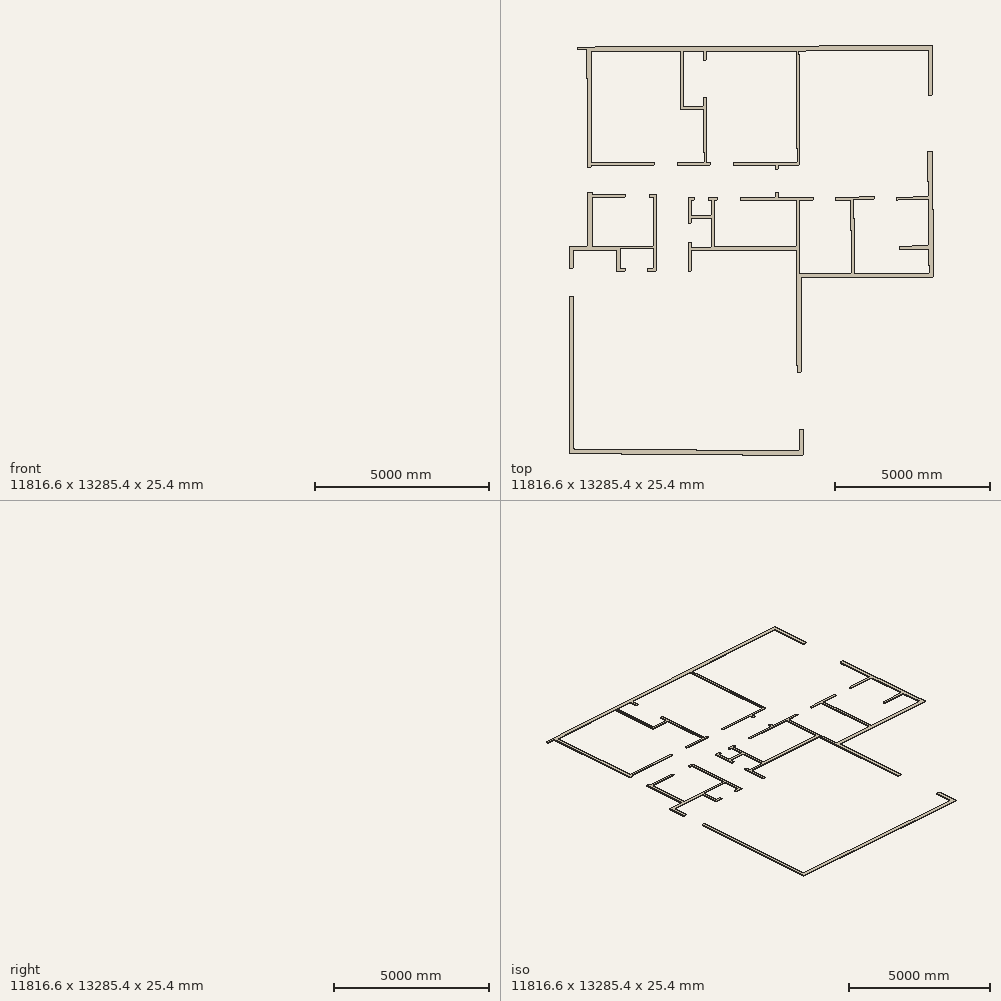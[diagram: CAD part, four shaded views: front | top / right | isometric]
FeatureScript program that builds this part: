
annotation { "Feature Type Name" : "Feature", "Feature Type Description" : "" }
export const myFeature = defineFeature(function(context is Context, id is Id, definition is map)
    precondition{}
    {
        {
            var Q0;
            Q0=qCreatedBy(makeId("Top.planeOp"),FACE);
            var sketch = newSketch(context, id + "F0", { "sketchPlane" : qUnion([Q0])});
            skLineSegment(sketch, "E0", {"start": v(-3431.17, -188.14) * mm, "end": v(3883.78, -248.2) * mm});
            skLineSegment(sketch, "E1", {"start": v(-3431.17, -188.14) * mm, "end": v(-3431.17, 4762.64) * mm});
            skLineSegment(sketch, "E2", {"start": v(-3568.5, 4762.64) * mm, "end": v(-3568.5, -336.6) * mm});
            skLineSegment(sketch, "E3", {"start": v(-3568.5, -336.6) * mm, "end": v(4029.87, -399) * mm});
            skLineSegment(sketch, "E4", {"start": v(4029.87, -399) * mm, "end": v(4029.87, 458) * mm});
            skLineSegment(sketch, "E5", {"start": v(4029.87, 458) * mm, "end": v(3883.78, 459.2) * mm});
            skLineSegment(sketch, "E6", {"start": v(3883.78, -248.2) * mm, "end": v(3883.78, 459.2) * mm});
            skLineSegment(sketch, "E7", {"start": v(-3568.5, 4762.64) * mm, "end": v(-3431.17, 4762.64) * mm});
            skLineSegment(sketch, "E8", {"start": v(-3577.11, 5654.75) * mm, "end": v(-3441.63, 5654.75) * mm});
            skLineSegment(sketch, "E9", {"start": v(-3441.63, 5654.75) * mm, "end": v(-3441.63, 6255.3) * mm});
            skLineSegment(sketch, "E10", {"start": v(-3441.63, 6255.3) * mm, "end": v(-2039.15, 6255.3) * mm});
            skLineSegment(sketch, "E11", {"start": v(-2039.15, 6255.3) * mm, "end": v(-2039.15, 5570.53) * mm});
            skLineSegment(sketch, "E12", {"start": v(-2039.15, 5570.53) * mm, "end": v(-1759.02, 5570.53) * mm});
            skLineSegment(sketch, "E13", {"start": v(-1759.02, 5570.53) * mm, "end": v(-1759.02, 5667.57) * mm});
            skLineSegment(sketch, "E14", {"start": v(-1759.02, 5667.57) * mm, "end": v(-1925.63, 5667.57) * mm});
            skLineSegment(sketch, "E15", {"start": v(-1925.63, 5667.57) * mm, "end": v(-1925.63, 6301.06) * mm});
            skLineSegment(sketch, "E16", {"start": v(-1925.63, 6301.06) * mm, "end": v(-847.22, 6301.06) * mm});
            skLineSegment(sketch, "E17", {"start": v(-847.22, 6301.06) * mm, "end": v(-847.22, 5667.57) * mm});
            skLineSegment(sketch, "E18", {"start": v(-847.22, 5667.57) * mm, "end": v(-1022.99, 5667.57) * mm});
            skLineSegment(sketch, "E19", {"start": v(-1022.99, 5667.57) * mm, "end": v(-1022.99, 5574.2) * mm});
            skLineSegment(sketch, "E20", {"start": v(-1022.99, 5574.2) * mm, "end": v(-755.67, 5574.2) * mm});
            skLineSegment(sketch, "E21", {"start": v(-755.67, 5574.2) * mm, "end": v(-755.67, 8062.4) * mm});
            skLineSegment(sketch, "E22", {"start": v(-755.67, 8062.4) * mm, "end": v(-964.4, 8062.4) * mm});
            skLineSegment(sketch, "E23", {"start": v(-964.4, 8062.4) * mm, "end": v(-964.4, 7972.69) * mm});
            skLineSegment(sketch, "E24", {"start": v(-964.4, 7972.69) * mm, "end": v(-850.88, 7972.69) * mm});
            skLineSegment(sketch, "E25", {"start": v(-850.88, 7972.69) * mm, "end": v(-850.88, 6388.47) * mm});
            skLineSegment(sketch, "E26", {"start": v(-850.88, 6388.47) * mm, "end": v(-2831.49, 6388.47) * mm});
            skLineSegment(sketch, "E27", {"start": v(-2831.49, 6388.47) * mm, "end": v(-2831.49, 7972.69) * mm});
            skLineSegment(sketch, "E28", {"start": v(-2831.49, 7972.69) * mm, "end": v(-1753.73, 7972.69) * mm});
            skLineSegment(sketch, "E29", {"start": v(-1753.73, 7972.69) * mm, "end": v(-1753.73, 8062.4) * mm});
            skLineSegment(sketch, "E30", {"start": v(-1753.73, 8062.4) * mm, "end": v(-2831.49, 8062.4) * mm});
            skLineSegment(sketch, "E31", {"start": v(-2831.49, 8062.4) * mm, "end": v(-2831.49, 8138.6) * mm});
            skLineSegment(sketch, "E32", {"start": v(-2831.49, 8138.6) * mm, "end": v(-2973.3, 8138.6) * mm});
            skLineSegment(sketch, "E33", {"start": v(-2973.3, 8138.6) * mm, "end": v(-2973.3, 6388.47) * mm});
            skLineSegment(sketch, "E34", {"start": v(-2973.3, 6388.47) * mm, "end": v(-3577.11, 6388.47) * mm});
            skLineSegment(sketch, "E35", {"start": v(-3577.11, 6388.47) * mm, "end": v(-3577.11, 5654.75) * mm});
            skLineSegment(sketch, "E36", {"start": v(3806.17, 2284.05) * mm, "end": v(3953.5, 2284.05) * mm});
            skLineSegment(sketch, "E37", {"start": v(3953.5, 2284.05) * mm, "end": v(3953.5, 5361.25) * mm});
            skLineSegment(sketch, "E38", {"start": v(3953.5, 5361.25) * mm, "end": v(8239.48, 5361.25) * mm});
            skLineSegment(sketch, "E39", {"start": v(8239.48, 5361.25) * mm, "end": v(8189.25, 9456.38) * mm});
            skLineSegment(sketch, "E40", {"start": v(8189.25, 9456.38) * mm, "end": v(8038.6, 9454.53) * mm});
            skLineSegment(sketch, "E41", {"start": v(8038.6, 9454.53) * mm, "end": v(8056.64, 7983.25) * mm});
            skLineSegment(sketch, "E42", {"start": v(8056.64, 7983.25) * mm, "end": v(7020.93, 7970.55) * mm});
            skLineSegment(sketch, "E43", {"start": v(7020.93, 7970.55) * mm, "end": v(7022.05, 7879.33) * mm});
            skLineSegment(sketch, "E44", {"start": v(7022.05, 7879.33) * mm, "end": v(8056.64, 7892.01) * mm});
            skLineSegment(sketch, "E45", {"start": v(8056.64, 7892.01) * mm, "end": v(8075, 6396.03) * mm});
            skLineSegment(sketch, "E46", {"start": v(8075, 6396.03) * mm, "end": v(7131.33, 6384.46) * mm});
            skLineSegment(sketch, "E47", {"start": v(7131.33, 6384.46) * mm, "end": v(7132.47, 6292.09) * mm});
            skLineSegment(sketch, "E48", {"start": v(7132.47, 6292.09) * mm, "end": v(8056.64, 6292.09) * mm});
            skLineSegment(sketch, "E49", {"start": v(8056.64, 6292.09) * mm, "end": v(8095.5, 5495.19) * mm});
            skLineSegment(sketch, "E50", {"start": v(8095.5, 5495.19) * mm, "end": v(5674.59, 5495.19) * mm});
            skLineSegment(sketch, "E51", {"start": v(5674.59, 5495.19) * mm, "end": v(5645.19, 7892.01) * mm});
            skLineSegment(sketch, "E52", {"start": v(5645.19, 7892.01) * mm, "end": v(6304.1, 7892.01) * mm});
            skLineSegment(sketch, "E53", {"start": v(6304.1, 7892.01) * mm, "end": v(6302.97, 7983.25) * mm});
            skLineSegment(sketch, "E54", {"start": v(6302.97, 7983.25) * mm, "end": v(5059.47, 7968) * mm});
            skLineSegment(sketch, "E55", {"start": v(5059.47, 7968) * mm, "end": v(5060.58, 7878.2) * mm});
            skLineSegment(sketch, "E56", {"start": v(5060.58, 7878.2) * mm, "end": v(5543.43, 7878.2) * mm});
            skLineSegment(sketch, "E57", {"start": v(5543.43, 7878.2) * mm, "end": v(5572.66, 5495.19) * mm});
            skLineSegment(sketch, "E58", {"start": v(5572.66, 5495.19) * mm, "end": v(3901.21, 5495.19) * mm});
            skLineSegment(sketch, "E59", {"start": v(3901.21, 5495.19) * mm, "end": v(3882.25, 7873.19) * mm});
            skLineSegment(sketch, "E60", {"start": v(3882.25, 7873.19) * mm, "end": v(4356.11, 7879) * mm});
            skLineSegment(sketch, "E61", {"start": v(4356.11, 7879) * mm, "end": v(4355.02, 7967.98) * mm});
            skLineSegment(sketch, "E62", {"start": v(4355.02, 7967.98) * mm, "end": v(3197.25, 7967.98) * mm});
            skLineSegment(sketch, "E63", {"start": v(3197.25, 7967.98) * mm, "end": v(3195.39, 8119.58) * mm});
            skLineSegment(sketch, "E64", {"start": v(3195.39, 8119.58) * mm, "end": v(3102.47, 8118.44) * mm});
            skLineSegment(sketch, "E65", {"start": v(3102.47, 8118.44) * mm, "end": v(3102.47, 7967.98) * mm});
            skLineSegment(sketch, "E66", {"start": v(3102.47, 7967.98) * mm, "end": v(1985.22, 7967.98) * mm});
            skLineSegment(sketch, "E67", {"start": v(1985.22, 7967.98) * mm, "end": v(1986.3, 7879) * mm});
            skLineSegment(sketch, "E68", {"start": v(1986.3, 7879) * mm, "end": v(3790, 7873.19) * mm});
            skLineSegment(sketch, "E69", {"start": v(3790, 7873.19) * mm, "end": v(3790, 6384.46) * mm});
            skLineSegment(sketch, "E70", {"start": v(3790, 6384.46) * mm, "end": v(1127.2, 6384.46) * mm});
            skLineSegment(sketch, "E71", {"start": v(1127.2, 6384.46) * mm, "end": v(1127.2, 7873.19) * mm});
            skLineSegment(sketch, "E72", {"start": v(1127.2, 7873.19) * mm, "end": v(1231.35, 7873.19) * mm});
            skLineSegment(sketch, "E73", {"start": v(1231.35, 7873.19) * mm, "end": v(1230.2, 7967.98) * mm});
            skLineSegment(sketch, "E74", {"start": v(1230.2, 7967.98) * mm, "end": v(931.65, 7967.98) * mm});
            skLineSegment(sketch, "E75", {"start": v(931.65, 7967.98) * mm, "end": v(932.82, 7873.19) * mm});
            skLineSegment(sketch, "E76", {"start": v(932.82, 7873.19) * mm, "end": v(1029.43, 7873.19) * mm});
            skLineSegment(sketch, "E77", {"start": v(1029.43, 7873.19) * mm, "end": v(1035.46, 7381.09) * mm});
            skLineSegment(sketch, "E78", {"start": v(1035.46, 7381.09) * mm, "end": v(389.64, 7381.09) * mm});
            skLineSegment(sketch, "E79", {"start": v(389.64, 7381.09) * mm, "end": v(389.64, 7873.19) * mm});
            skLineSegment(sketch, "E80", {"start": v(389.64, 7873.19) * mm, "end": v(490.6, 7873.19) * mm});
            skLineSegment(sketch, "E81", {"start": v(490.6, 7873.19) * mm, "end": v(489.44, 7967.98) * mm});
            skLineSegment(sketch, "E82", {"start": v(489.44, 7967.98) * mm, "end": v(290.8, 7967.98) * mm});
            skLineSegment(sketch, "E83", {"start": v(290.8, 7967.98) * mm, "end": v(301.4, 7104.7) * mm});
            skLineSegment(sketch, "E84", {"start": v(301.4, 7104.7) * mm, "end": v(391.77, 7104.7) * mm});
            skLineSegment(sketch, "E85", {"start": v(391.77, 7104.7) * mm, "end": v(391.77, 7288.53) * mm});
            skLineSegment(sketch, "E86", {"start": v(391.77, 7288.53) * mm, "end": v(1035.46, 7288.53) * mm});
            skLineSegment(sketch, "E87", {"start": v(1035.46, 7288.53) * mm, "end": v(1035.46, 6337.35) * mm});
            skLineSegment(sketch, "E88", {"start": v(1035.46, 6337.35) * mm, "end": v(398.15, 6337.35) * mm});
            skLineSegment(sketch, "E89", {"start": v(398.15, 6337.35) * mm, "end": v(398.15, 6514.83) * mm});
            skLineSegment(sketch, "E90", {"start": v(398.15, 6514.83) * mm, "end": v(299.3, 6514.83) * mm});
            skLineSegment(sketch, "E91", {"start": v(299.3, 6514.83) * mm, "end": v(299.3, 5548.78) * mm});
            skLineSegment(sketch, "E92", {"start": v(299.3, 5548.78) * mm, "end": v(389.64, 5548.78) * mm});
            skLineSegment(sketch, "E93", {"start": v(389.64, 5548.78) * mm, "end": v(389.64, 6241.26) * mm});
            skLineSegment(sketch, "E94", {"start": v(389.64, 6241.26) * mm, "end": v(3796.45, 6241.26) * mm});
            skLineSegment(sketch, "E95", {"start": v(3796.45, 6241.26) * mm, "end": v(3806.17, 2284.05) * mm});
            skLineSegment(sketch, "E96", {"start": v(8192.58, 11266.77) * mm, "end": v(8192.58, 12886.43) * mm});
            skLineSegment(sketch, "E97", {"start": v(8192.58, 12886.43) * mm, "end": v(-3307.1, 12835.22) * mm});
            skLineSegment(sketch, "E98", {"start": v(-3307.1, 12835.22) * mm, "end": v(-3306.7, 12742.3) * mm});
            skLineSegment(sketch, "E99", {"start": v(-3306.7, 12742.3) * mm, "end": v(-3003.28, 12743.65) * mm});
            skLineSegment(sketch, "E100", {"start": v(-3003.28, 12743.65) * mm, "end": v(-2986.3, 8931.63) * mm});
            skLineSegment(sketch, "E101", {"start": v(-2986.3, 8931.63) * mm, "end": v(-2845.97, 8932.25) * mm});
            skLineSegment(sketch, "E102", {"start": v(-2845.97, 8932.25) * mm, "end": v(-2846.3, 9006.7) * mm});
            skLineSegment(sketch, "E103", {"start": v(-2846.3, 9006.7) * mm, "end": v(-814.6, 8993.72) * mm});
            skLineSegment(sketch, "E104", {"start": v(-814.6, 8993.72) * mm, "end": v(-814.6, 9082.4) * mm});
            skLineSegment(sketch, "E105", {"start": v(-814.6, 9082.4) * mm, "end": v(-2846.3, 9094.41) * mm});
            skLineSegment(sketch, "E106", {"start": v(-2846.3, 9094.41) * mm, "end": v(-2862.3, 12686.1) * mm});
            skLineSegment(sketch, "E107", {"start": v(-2862.3, 12686.1) * mm, "end": v(36.38, 12699) * mm});
            skLineSegment(sketch, "E108", {"start": v(36.38, 12699) * mm, "end": v(36.38, 10809.33) * mm});
            skLineSegment(sketch, "E109", {"start": v(36.38, 10809.33) * mm, "end": v(779.48, 10812.64) * mm});
            skLineSegment(sketch, "E110", {"start": v(779.48, 10812.64) * mm, "end": v(795.05, 9096.67) * mm});
            skLineSegment(sketch, "E111", {"start": v(795.05, 9096.67) * mm, "end": v(-63.77, 9092.84) * mm});
            skLineSegment(sketch, "E112", {"start": v(-63.77, 9092.84) * mm, "end": v(-63.38, 9006.7) * mm});
            skLineSegment(sketch, "E113", {"start": v(-63.38, 9006.7) * mm, "end": v(997.02, 9000.15) * mm});
            skLineSegment(sketch, "E114", {"start": v(997.02, 9000.15) * mm, "end": v(996.59, 9097.56) * mm});
            skLineSegment(sketch, "E115", {"start": v(996.59, 9097.56) * mm, "end": v(880.84, 9096.67) * mm});
            skLineSegment(sketch, "E116", {"start": v(880.84, 9096.67) * mm, "end": v(871.5, 11193.23) * mm});
            skLineSegment(sketch, "E117", {"start": v(871.5, 11193.23) * mm, "end": v(782.54, 11192.83) * mm});
            skLineSegment(sketch, "E118", {"start": v(782.54, 11192.83) * mm, "end": v(783.85, 10897.42) * mm});
            skLineSegment(sketch, "E119", {"start": v(783.85, 10897.42) * mm, "end": v(129.28, 10894.5) * mm});
            skLineSegment(sketch, "E120", {"start": v(129.28, 10894.5) * mm, "end": v(129.28, 12699) * mm});
            skLineSegment(sketch, "E121", {"start": v(129.28, 12699) * mm, "end": v(777.18, 12699) * mm});
            skLineSegment(sketch, "E122", {"start": v(777.18, 12699) * mm, "end": v(778.51, 12398.78) * mm});
            skLineSegment(sketch, "E123", {"start": v(778.51, 12398.78) * mm, "end": v(868.33, 12399.18) * mm});
            skLineSegment(sketch, "E124", {"start": v(868.33, 12399.18) * mm, "end": v(868.33, 12699) * mm});
            skLineSegment(sketch, "E125", {"start": v(868.33, 12699) * mm, "end": v(3780.6, 12706.6) * mm});
            skLineSegment(sketch, "E126", {"start": v(3780.6, 12706.6) * mm, "end": v(3809.2, 9096.67) * mm});
            skLineSegment(sketch, "E127", {"start": v(3809.2, 9096.67) * mm, "end": v(1744.7, 9096.67) * mm});
            skLineSegment(sketch, "E128", {"start": v(1744.7, 9096.67) * mm, "end": v(1745.1, 9006.7) * mm});
            skLineSegment(sketch, "E129", {"start": v(1745.1, 9006.7) * mm, "end": v(3101.76, 9006.7) * mm});
            skLineSegment(sketch, "E130", {"start": v(3101.76, 9006.7) * mm, "end": v(3102.39, 8865.28) * mm});
            skLineSegment(sketch, "E131", {"start": v(3102.39, 8865.28) * mm, "end": v(3194.19, 8865.7) * mm});
            skLineSegment(sketch, "E132", {"start": v(3194.19, 8865.7) * mm, "end": v(3194.19, 9006.7) * mm});
            skLineSegment(sketch, "E133", {"start": v(3194.19, 9006.7) * mm, "end": v(3895.32, 9009.82) * mm});
            skLineSegment(sketch, "E134", {"start": v(3895.32, 9009.82) * mm, "end": v(3869.62, 12706.6) * mm});
            skLineSegment(sketch, "E135", {"start": v(3869.62, 12706.6) * mm, "end": v(8054.19, 12735.7) * mm});
            skLineSegment(sketch, "E136", {"start": v(8054.19, 12735.7) * mm, "end": v(8054.19, 11266.77) * mm});
            skLineSegment(sketch, "E137", {"start": v(8054.19, 11266.77) * mm, "end": v(8192.58, 11266.77) * mm});
            skSolve(sketch);
        }
        {
            var Q0;
            Q0=makeQuery(id+"F0.imprint","IMPRINT",FACE,{"disambiguationData":[TD([[makeQuery(id+"F0.imprint","IMPRINT",EDGE,{"derivedFrom":sQuery(id+"F0.wireOp",EDGE,"E8")}),1.0]])]});
            extrude(context, id + "F1", {"entities" : qUnion([Q0]), "depth" : 25.4 * mm, "offsetDistance" : 25.4 * mm});
        }
        {
            var Q0;
            Q0=makeQuery(id+"F0.imprint","IMPRINT",FACE,{"disambiguationData":[TD([[makeQuery(id+"F0.imprint","IMPRINT",EDGE,{"derivedFrom":sQuery(id+"F0.wireOp",EDGE,"E0")}),-1.0]])]});
            extrude(context, id + "F2", {"entities" : qUnion([Q0]), "depth" : 25.4 * mm, "offsetDistance" : 25.4 * mm});
        }
        {
            var Q0;
            Q0=makeQuery(id+"F0.imprint","IMPRINT",FACE,{"disambiguationData":[TD([[makeQuery(id+"F0.imprint","IMPRINT",EDGE,{"derivedFrom":sQuery(id+"F0.wireOp",EDGE,"E36")}),1.0]])]});
            extrude(context, id + "F3", {"entities" : qUnion([Q0]), "depth" : 25.4 * mm, "offsetDistance" : 25.4 * mm});
        }
        {
            var Q0;
            Q0=makeQuery(id+"F0.imprint","IMPRINT",FACE,{"disambiguationData":[TD([[makeQuery(id+"F0.imprint","IMPRINT",EDGE,{"derivedFrom":sQuery(id+"F0.wireOp",EDGE,"E96")}),1.0]])]});
            extrude(context, id + "F4", {"entities" : qUnion([Q0]), "depth" : 25.4 * mm, "offsetDistance" : 25.4 * mm});
        }
    });
